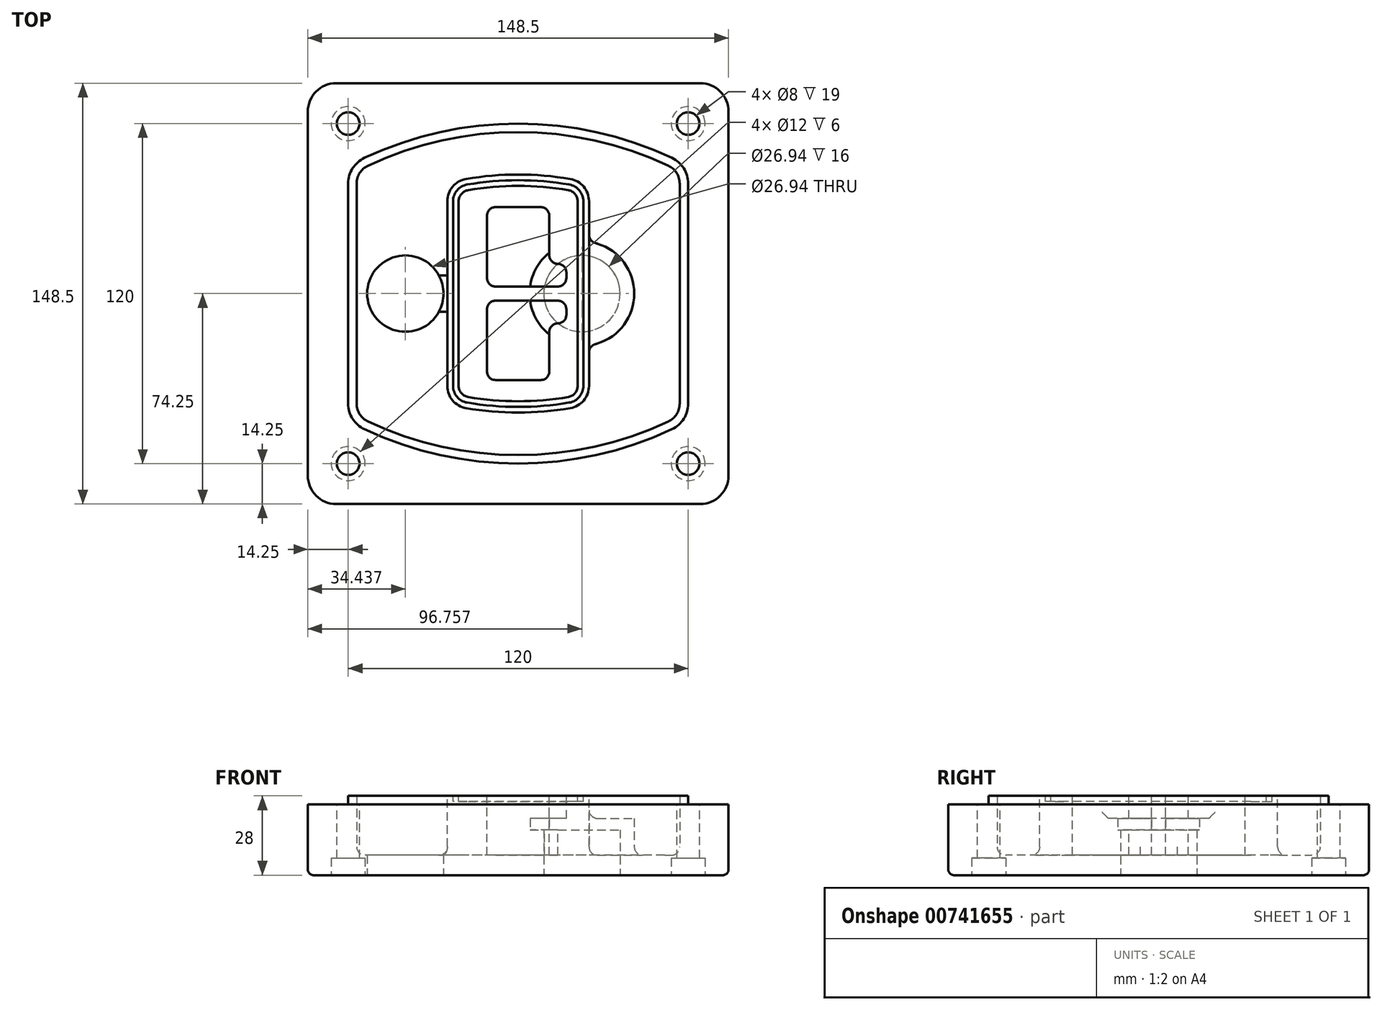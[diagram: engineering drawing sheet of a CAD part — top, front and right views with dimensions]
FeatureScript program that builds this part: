
annotation { "Feature Type Name" : "Feature", "Feature Type Description" : "" }
export const myFeature = defineFeature(function(context is Context, id is Id, definition is map)
    precondition{}
    {
        {
            var Q0;
            Q0=qCreatedBy(makeId("Top.planeOp"),FACE);
            var sketch = newSketch(context, id + "F0", { "sketchPlane" : qUnion([Q0])});
            skPoint(sketch, "E0.rect.middle", {"position": v(0, 0) * mm});
            skLineSegment(sketch, "E1.bottom", {"start": v(-64.25, -74.25) * mm, "end": v(64.25, -74.25) * mm});
            skLineSegment(sketch, "E1.top", {"start": v(-64.25, 74.25) * mm, "end": v(64.25, 74.25) * mm});
            skLineSegment(sketch, "E1.left", {"start": v(-74.25, -64.25) * mm, "end": v(-74.25, 64.25) * mm});
            skLineSegment(sketch, "E1.right", {"start": v(74.25, -64.25) * mm, "end": v(74.25, 64.25) * mm});
            skLineSegment(sketch, "E2", {"start": v(-74.25, 74.25) * mm, "end": v(74.25, -74.25) * mm, "construction": true});
            skLineSegment(sketch, "E3", {"start": v(74.25, 74.25) * mm, "end": v(-74.25, -74.25) * mm, "construction": true});
            skCircle(sketch, "E4", {"center": v(-60, 60) * mm, "radius": 4 * mm});
            skCircle(sketch, "E5", {"center": v(60, 60) * mm, "radius": 4 * mm});
            skCircle(sketch, "E6", {"center": v(60, -60) * mm, "radius": 4 * mm});
            skCircle(sketch, "E7", {"center": v(-60, -60) * mm, "radius": 4 * mm});
            skLineSegment(sketch, "E8", {"start": v(-60, 60) * mm, "end": v(60, 60) * mm, "construction": true});
            skLineSegment(sketch, "E9", {"start": v(60, 60) * mm, "end": v(60, -60) * mm, "construction": true});
            skLineSegment(sketch, "E10", {"start": v(60, -60) * mm, "end": v(-60, -60) * mm, "construction": true});
            skLineSegment(sketch, "E11", {"start": v(-60, -60) * mm, "end": v(-60, 60) * mm, "construction": true});
            skLineSegment(sketch, "E12", {"start": v(-60, 38.83) * mm, "end": v(-60, -38.83) * mm});
            skLineSegment(sketch, "E13", {"start": v(60, 38.83) * mm, "end": v(60, -38.83) * mm});
            skArc(sketch, "E14", {"start": v(54.26, 47.88) * mm, "mid": v(0, 60) * mm, "end": v(-54.26, 47.88) * mm});
            skArc(sketch, "E15", {"start": v(-54.26, -47.88) * mm, "mid": v(0, -60) * mm, "end": v(54.26, -47.88) * mm});
            skLineSegment(sketch, "E16", {"start": v(-60, 0) * mm, "end": v(60, 0) * mm, "construction": true});
            skPoint(sketch, "E17.visualSharp", {"position": v(-60, -45) * mm});
            skArc(sketch, "E17.filletArc", {"start": v(-60, -38.83) * mm, "mid": v(-58.44, -44.2) * mm, "end": v(-54.26, -47.88) * mm});
            skPoint(sketch, "E18.visualSharp", {"position": v(-60, 45) * mm});
            skArc(sketch, "E18.filletArc", {"start": v(-54.26, 47.88) * mm, "mid": v(-58.44, 44.2) * mm, "end": v(-60, 38.83) * mm});
            skPoint(sketch, "E19.visualSharp", {"position": v(60, 45) * mm});
            skArc(sketch, "E19.filletArc", {"start": v(60, 38.83) * mm, "mid": v(58.44, 44.2) * mm, "end": v(54.26, 47.88) * mm});
            skPoint(sketch, "E20.visualSharp", {"position": v(60, -45) * mm});
            skArc(sketch, "E20.filletArc", {"start": v(54.26, -47.88) * mm, "mid": v(58.44, -44.2) * mm, "end": v(60, -38.83) * mm});
            skPoint(sketch, "E21.visualSharp", {"position": v(-74.25, 74.25) * mm});
            skArc(sketch, "E21.filletArc", {"start": v(-64.25, 74.25) * mm, "mid": v(-71.32, 71.32) * mm, "end": v(-74.25, 64.25) * mm});
            skPoint(sketch, "E22.visualSharp", {"position": v(74.25, 74.25) * mm});
            skArc(sketch, "E22.filletArc", {"start": v(74.25, 64.25) * mm, "mid": v(71.32, 71.32) * mm, "end": v(64.25, 74.25) * mm});
            skPoint(sketch, "E23.visualSharp", {"position": v(74.25, -74.25) * mm});
            skArc(sketch, "E23.filletArc", {"start": v(64.25, -74.25) * mm, "mid": v(71.32, -71.32) * mm, "end": v(74.25, -64.25) * mm});
            skPoint(sketch, "E24.visualSharp", {"position": v(-74.25, -74.25) * mm});
            skArc(sketch, "E24.filletArc", {"start": v(-74.25, -64.25) * mm, "mid": v(-71.32, -71.32) * mm, "end": v(-64.25, -74.25) * mm});
            skArc(sketch, "E25.0", {"start": v(57, 38.83) * mm, "mid": v(55.9, 42.58) * mm, "end": v(52.98, 45.17) * mm});
            skLineSegment(sketch, "E25.1", {"start": v(57, 38.83) * mm, "end": v(57, -38.83) * mm});
            skArc(sketch, "E25.2", {"start": v(52.98, -45.17) * mm, "mid": v(55.9, -42.58) * mm, "end": v(57, -38.83) * mm});
            skArc(sketch, "E25.3", {"start": v(-52.98, -45.17) * mm, "mid": v(0, -57) * mm, "end": v(52.98, -45.17) * mm});
            skArc(sketch, "E25.4", {"start": v(-57, -38.83) * mm, "mid": v(-55.9, -42.58) * mm, "end": v(-52.98, -45.17) * mm});
            skArc(sketch, "E25.5", {"start": v(52.98, 45.17) * mm, "mid": v(0, 57) * mm, "end": v(-52.98, 45.17) * mm});
            skLineSegment(sketch, "E25.6", {"start": v(-57, 38.83) * mm, "end": v(-57, -38.83) * mm});
            skArc(sketch, "E25.7", {"start": v(-52.98, 45.17) * mm, "mid": v(-55.9, 42.58) * mm, "end": v(-57, 38.83) * mm});
            skArc(sketch, "E26.0", {"start": v(-55.96, 51.5) * mm, "mid": v(-61.82, 46.33) * mm, "end": v(-64, 38.83) * mm});
            skArc(sketch, "E26.1", {"start": v(55.96, 51.5) * mm, "mid": v(0, 64) * mm, "end": v(-55.96, 51.5) * mm});
            skArc(sketch, "E26.2", {"start": v(64, 38.83) * mm, "mid": v(61.82, 46.33) * mm, "end": v(55.96, 51.5) * mm});
            skLineSegment(sketch, "E26.3", {"start": v(64, 38.83) * mm, "end": v(64, -38.83) * mm});
            skArc(sketch, "E26.4", {"start": v(55.96, -51.5) * mm, "mid": v(61.82, -46.33) * mm, "end": v(64, -38.83) * mm});
            skLineSegment(sketch, "E26.5", {"start": v(-64, 38.83) * mm, "end": v(-64, -38.83) * mm});
            skArc(sketch, "E26.6", {"start": v(-55.96, -51.5) * mm, "mid": v(0, -64) * mm, "end": v(55.96, -51.5) * mm});
            skArc(sketch, "E26.7", {"start": v(-64, -38.83) * mm, "mid": v(-61.82, -46.33) * mm, "end": v(-55.96, -51.5) * mm});
            skSolve(sketch);
        }
        {
            var Q0;
            Q0=makeQuery(id+"F0.imprint","IMPRINT",FACE,{"disambiguationData":[TD([[makeQuery(id+"F0.imprint","IMPRINT",EDGE,{"derivedFrom":sQuery(id+"F0.wireOp",EDGE,"E1.bottom")}),1.0]])]});
            var Q1;
            Q1=makeQuery(id+"F0.imprint","IMPRINT",FACE,{"disambiguationData":[TD([[makeQuery(id+"F0.imprint","IMPRINT",EDGE,{"derivedFrom":sQuery(id+"F0.wireOp",EDGE,"E12")}),1.0]])]});
            var Q2;
            Q2=makeQuery(id+"F0.imprint","IMPRINT",FACE,{"disambiguationData":[TD([[makeQuery(id+"F0.imprint","IMPRINT",EDGE,{"derivedFrom":sQuery(id+"F0.wireOp",EDGE,"E25.0")}),1.0]])]});
            var Q3;
            Q3=makeQuery(id+"F0.imprint","IMPRINT",FACE,{"disambiguationData":[TD([[makeQuery(id+"F0.imprint","IMPRINT",EDGE,{"derivedFrom":sQuery(id+"F0.wireOp",EDGE,"E12")}),-1.0]])]});
            extrude(context, id + "F1", {"entities" : qUnion([Q0, Q1, Q2, Q3]), "oppositeDirection" : true, "depth" : 25 * mm, "offsetDistance" : 25 * mm});
        }
        {
            var Q0;
            Q0=makeQuery(id+"F0.imprint","IMPRINT",FACE,{"disambiguationData":[TD([[makeQuery(id+"F0.imprint","IMPRINT",EDGE,{"derivedFrom":sQuery(id+"F0.wireOp",EDGE,"E12")}),1.0]])]});
            extrude(context, id + "F2", {"entities" : qUnion([Q0]), "operationType" : NewBodyOperationType.ADD, "depth" : 3 * mm, "offsetDistance" : 25 * mm});
        }
        {
            var Q0;
            Q0=makeQuery(id+"F0.imprint","IMPRINT",FACE,{"disambiguationData":[TD([[makeQuery(id+"F0.imprint","IMPRINT",EDGE,{"derivedFrom":sQuery(id+"F0.wireOp",EDGE,"E25.0")}),1.0]])]});
            extrude(context, id + "F3", {"entities" : qUnion([Q0]), "operationType" : NewBodyOperationType.REMOVE, "oppositeDirection" : true, "depth" : 18 * mm, "offsetDistance" : 25 * mm});
        }
        {
            var Q0;
            Q0=makeQuery(id+"F2.opExtrude","CAP_FACE",FACE,{"disambiguationData":[OSD([sQuery(id+"F0.wireOp",EDGE,"E12"),sQuery(id+"F0.wireOp",EDGE,"E13"),sQuery(id+"F0.wireOp",EDGE,"E14"),sQuery(id+"F0.wireOp",EDGE,"E15"),sQuery(id+"F0.wireOp",EDGE,"E17.filletArc"),sQuery(id+"F0.wireOp",EDGE,"E18.filletArc"),sQuery(id+"F0.wireOp",EDGE,"E19.filletArc"),sQuery(id+"F0.wireOp",EDGE,"E20.filletArc"),sQuery(id+"F0.wireOp",EDGE,"E25.0"),sQuery(id+"F0.wireOp",EDGE,"E25.1"),sQuery(id+"F0.wireOp",EDGE,"E25.2"),sQuery(id+"F0.wireOp",EDGE,"E25.3"),sQuery(id+"F0.wireOp",EDGE,"E25.4"),sQuery(id+"F0.wireOp",EDGE,"E25.5"),sQuery(id+"F0.wireOp",EDGE,"E25.6"),sQuery(id+"F0.wireOp",EDGE,"E25.7")])],"isStart":false});
            var sketch = newSketch(context, id + "F4", { "sketchPlane" : qUnion([Q0])});
            skArc(sketch, "E27.0", {"start": v(-18.34, -40.45) * mm, "mid": v(0, -42) * mm, "end": v(18.34, -40.45) * mm});
            skArc(sketch, "E28.0", {"start": v(18.34, 40.45) * mm, "mid": v(0, 42) * mm, "end": v(-18.34, 40.45) * mm});
            skLineSegment(sketch, "E29", {"start": v(-25, 32.57) * mm, "end": v(-25, -32.57) * mm});
            skLineSegment(sketch, "E30", {"start": v(25, 32.57) * mm, "end": v(25, -32.57) * mm});
            skLineSegment(sketch, "E31", {"start": v(-25, 39.1) * mm, "end": v(25, 39.1) * mm, "construction": true});
            skLineSegment(sketch, "E32", {"start": v(-25, -39.1) * mm, "end": v(25, -39.1) * mm, "construction": true});
            skPoint(sketch, "E33.visualSharp", {"position": v(-25, 39.1) * mm});
            skArc(sketch, "E33.filletArc", {"start": v(-18.34, 40.45) * mm, "mid": v(-23.11, 37.73) * mm, "end": v(-25, 32.57) * mm});
            skPoint(sketch, "E34.visualSharp", {"position": v(25, 39.1) * mm});
            skArc(sketch, "E34.filletArc", {"start": v(25, 32.57) * mm, "mid": v(23.11, 37.73) * mm, "end": v(18.34, 40.45) * mm});
            skPoint(sketch, "E35.visualSharp", {"position": v(25, -39.1) * mm});
            skArc(sketch, "E35.filletArc", {"start": v(18.34, -40.45) * mm, "mid": v(23.11, -37.73) * mm, "end": v(25, -32.57) * mm});
            skPoint(sketch, "E36.visualSharp", {"position": v(-25, -39.1) * mm});
            skArc(sketch, "E36.filletArc", {"start": v(-25, -32.57) * mm, "mid": v(-23.11, -37.73) * mm, "end": v(-18.34, -40.45) * mm});
            skArc(sketch, "E37.0", {"start": v(52.98, 45.17) * mm, "mid": v(0, 57) * mm, "end": v(-52.98, 45.17) * mm});
            skArc(sketch, "E37.1", {"start": v(-52.98, 45.17) * mm, "mid": v(-55.9, 42.58) * mm, "end": v(-57, 38.83) * mm});
            skLineSegment(sketch, "E37.2", {"start": v(-57, 38.83) * mm, "end": v(-57, -38.83) * mm});
            skArc(sketch, "E37.3", {"start": v(-57, -38.83) * mm, "mid": v(-55.9, -42.58) * mm, "end": v(-52.98, -45.17) * mm});
            skArc(sketch, "E37.4", {"start": v(-52.98, -45.17) * mm, "mid": v(0, -57) * mm, "end": v(52.98, -45.17) * mm});
            skArc(sketch, "E37.5", {"start": v(52.98, -45.17) * mm, "mid": v(55.9, -42.58) * mm, "end": v(57, -38.83) * mm});
            skLineSegment(sketch, "E37.6", {"start": v(57, 38.83) * mm, "end": v(57, -38.83) * mm});
            skArc(sketch, "E37.7", {"start": v(57, 38.83) * mm, "mid": v(55.9, 42.58) * mm, "end": v(52.98, 45.17) * mm});
            skLineSegment(sketch, "E38.0", {"start": v(23, 32.57) * mm, "end": v(23, -32.57) * mm});
            skArc(sketch, "E38.1", {"start": v(18, -38.48) * mm, "mid": v(21.58, -36.44) * mm, "end": v(23, -32.57) * mm});
            skArc(sketch, "E38.2", {"start": v(-18, -38.48) * mm, "mid": v(0, -40) * mm, "end": v(18, -38.48) * mm});
            skArc(sketch, "E38.3", {"start": v(-23, -32.57) * mm, "mid": v(-21.58, -36.44) * mm, "end": v(-18, -38.48) * mm});
            skLineSegment(sketch, "E38.4", {"start": v(-23, 32.57) * mm, "end": v(-23, -32.57) * mm});
            skArc(sketch, "E38.5", {"start": v(23, 32.57) * mm, "mid": v(21.58, 36.44) * mm, "end": v(18, 38.48) * mm});
            skArc(sketch, "E38.6", {"start": v(-18, 38.48) * mm, "mid": v(-21.58, 36.44) * mm, "end": v(-23, 32.57) * mm});
            skArc(sketch, "E38.7", {"start": v(18, 38.48) * mm, "mid": v(0, 40) * mm, "end": v(-18, 38.48) * mm});
            skArc(sketch, "E39.0", {"start": v(21, 32.57) * mm, "mid": v(20.06, 35.15) * mm, "end": v(17.67, 36.5) * mm});
            skLineSegment(sketch, "E39.1", {"start": v(21, 32.57) * mm, "end": v(21, -32.57) * mm});
            skArc(sketch, "E39.2", {"start": v(17.67, -36.5) * mm, "mid": v(20.06, -35.15) * mm, "end": v(21, -32.57) * mm});
            skArc(sketch, "E39.3", {"start": v(-17.67, -36.5) * mm, "mid": v(0, -38) * mm, "end": v(17.67, -36.5) * mm});
            skArc(sketch, "E39.4", {"start": v(-21, -32.57) * mm, "mid": v(-20.06, -35.15) * mm, "end": v(-17.67, -36.5) * mm});
            skArc(sketch, "E39.5", {"start": v(17.67, 36.5) * mm, "mid": v(0, 38) * mm, "end": v(-17.67, 36.5) * mm});
            skLineSegment(sketch, "E39.6", {"start": v(-21, 32.57) * mm, "end": v(-21, -32.57) * mm});
            skArc(sketch, "E39.7", {"start": v(-17.67, 36.5) * mm, "mid": v(-20.06, 35.15) * mm, "end": v(-21, 32.57) * mm});
            skLineSegment(sketch, "E40", {"start": v(-25, 0) * mm, "end": v(25, 0) * mm, "construction": true});
            skLineSegment(sketch, "E41", {"start": v(-11, 5.5) * mm, "end": v(-11, 27.5) * mm});
            skLineSegment(sketch, "E42", {"start": v(-8, 30.5) * mm, "end": v(8, 30.5) * mm});
            skLineSegment(sketch, "E43", {"start": v(11, 27.5) * mm, "end": v(11, 13.5) * mm});
            skLineSegment(sketch, "E44", {"start": v(14, 10.5) * mm, "end": v(14, 10.5) * mm});
            skLineSegment(sketch, "E45", {"start": v(17, 7.5) * mm, "end": v(17, 5.5) * mm});
            skLineSegment(sketch, "E46", {"start": v(14, 2.5) * mm, "end": v(-8, 2.5) * mm});
            skPoint(sketch, "E47.visualSharp", {"position": v(-11, 30.5) * mm});
            skArc(sketch, "E47.filletArc", {"start": v(-8, 30.5) * mm, "mid": v(-10.12, 29.62) * mm, "end": v(-11, 27.5) * mm});
            skPoint(sketch, "E48.visualSharp", {"position": v(11, 30.5) * mm});
            skArc(sketch, "E48.filletArc", {"start": v(11, 27.5) * mm, "mid": v(10.12, 29.62) * mm, "end": v(8, 30.5) * mm});
            skPoint(sketch, "E49.visualSharp", {"position": v(11, 10.5) * mm});
            skArc(sketch, "E49.filletArc", {"start": v(11, 13.5) * mm, "mid": v(11.88, 11.38) * mm, "end": v(14, 10.5) * mm});
            skPoint(sketch, "E50.visualSharp", {"position": v(17, 10.5) * mm});
            skArc(sketch, "E50.filletArc", {"start": v(17, 7.5) * mm, "mid": v(16.12, 9.62) * mm, "end": v(14, 10.5) * mm});
            skPoint(sketch, "E51.visualSharp", {"position": v(17, 2.5) * mm});
            skArc(sketch, "E51.filletArc", {"start": v(14, 2.5) * mm, "mid": v(16.12, 3.38) * mm, "end": v(17, 5.5) * mm});
            skPoint(sketch, "E52.visualSharp", {"position": v(-11, 2.5) * mm});
            skArc(sketch, "E52.filletArc", {"start": v(-11, 5.5) * mm, "mid": v(-10.12, 3.38) * mm, "end": v(-8, 2.5) * mm});
            skLineSegment(sketch, "E53.0.MirrorCS", {"start": v(14, -2.5) * mm, "end": v(-8, -2.5) * mm});
            skArc(sketch, "E54.0.MirrorCS", {"start": v(-11, -5.5) * mm, "mid": v(-10.12, -3.38) * mm, "end": v(-8, -2.5) * mm});
            skLineSegment(sketch, "E55.0.MirrorCS", {"start": v(-11, -5.5) * mm, "end": v(-11, -27.5) * mm});
            skArc(sketch, "E56.0.MirrorCS", {"start": v(-8, -30.5) * mm, "mid": v(-10.12, -29.62) * mm, "end": v(-11, -27.5) * mm});
            skLineSegment(sketch, "E57.0.MirrorCS", {"start": v(-8, -30.5) * mm, "end": v(8, -30.5) * mm});
            skArc(sketch, "E58.0.MirrorCS", {"start": v(11, -27.5) * mm, "mid": v(10.12, -29.62) * mm, "end": v(8, -30.5) * mm});
            skLineSegment(sketch, "E59.0.MirrorCS", {"start": v(11, -27.5) * mm, "end": v(11, -13.5) * mm});
            skArc(sketch, "E60.0.MirrorCS", {"start": v(11, -13.5) * mm, "mid": v(11.88, -11.38) * mm, "end": v(14, -10.5) * mm});
            skArc(sketch, "E61.0.MirrorCS", {"start": v(17, -7.5) * mm, "mid": v(16.12, -9.62) * mm, "end": v(14, -10.5) * mm});
            skLineSegment(sketch, "E62.0.MirrorCS", {"start": v(17, -7.5) * mm, "end": v(17, -5.5) * mm});
            skArc(sketch, "E63.0.MirrorCS", {"start": v(14, -2.5) * mm, "mid": v(16.12, -3.38) * mm, "end": v(17, -5.5) * mm});
            skSolve(sketch);
        }
        {
            var Q0;
            Q0=makeQuery(id+"F4.imprint","IMPRINT",FACE,{"disambiguationData":[TD([[makeQuery(id+"F4.imprint","IMPRINT",EDGE,{"derivedFrom":sQuery(id+"F4.wireOp",EDGE,"E27.0")}),1.0]])]});
            var Q1;
            Q1=makeQuery(id+"F4.imprint","IMPRINT",FACE,{"disambiguationData":[TD([[makeQuery(id+"F4.imprint","IMPRINT",EDGE,{"derivedFrom":sQuery(id+"F4.wireOp",EDGE,"E38.0")}),-1.0]])]});
            var Q2;
            Q2=makeQuery(id+"F4.imprint","IMPRINT",FACE,{"disambiguationData":[TD([[makeQuery(id+"F4.imprint","IMPRINT",EDGE,{"derivedFrom":sQuery(id+"F4.wireOp",EDGE,"E39.0")}),1.0]])]});
            extrude(context, id + "F5", {"entities" : qUnion([Q0, Q1, Q2]), "operationType" : NewBodyOperationType.ADD, "endBound" : BoundingType.UP_TO_NEXT, "oppositeDirection" : true, "depth" : 25 * mm});
        }
        {
            var Q0;
            Q0=makeQuery(id+"F4.imprint","IMPRINT",FACE,{"disambiguationData":[TD([[makeQuery(id+"F4.imprint","IMPRINT",EDGE,{"derivedFrom":sQuery(id+"F4.wireOp",EDGE,"E38.0")}),-1.0]])]});
            extrude(context, id + "F6", {"entities" : qUnion([Q0]), "operationType" : NewBodyOperationType.REMOVE, "oppositeDirection" : true, "depth" : 2 * mm});
        }
        {
            var Q0;
            Q0=makeQuery(id+"F1.opExtrude","CAP_FACE",FACE,{"disambiguationData":[OSD([sQuery(id+"F0.wireOp",EDGE,"E1.bottom"),sQuery(id+"F0.wireOp",EDGE,"E1.top"),sQuery(id+"F0.wireOp",EDGE,"E1.left"),sQuery(id+"F0.wireOp",EDGE,"E1.right"),sQuery(id+"F0.wireOp",EDGE,"E4"),sQuery(id+"F0.wireOp",EDGE,"E5"),sQuery(id+"F0.wireOp",EDGE,"E6"),sQuery(id+"F0.wireOp",EDGE,"E7"),sQuery(id+"F0.wireOp",EDGE,"E21.filletArc"),sQuery(id+"F0.wireOp",EDGE,"E22.filletArc"),sQuery(id+"F0.wireOp",EDGE,"E23.filletArc"),sQuery(id+"F0.wireOp",EDGE,"E24.filletArc")])],"isStart":false});
            var sketch = newSketch(context, id + "F7", { "sketchPlane" : qUnion([Q0])});
            skCircle(sketch, "E64", {"center": v(22.5, 0) * mm, "radius": 13.47 * mm});
            skCircle(sketch, "E65", {"center": v(-39.81, 0) * mm, "radius": 13.47 * mm});
            skLineSegment(sketch, "E66", {"start": v(74.25, 0) * mm, "end": v(-74.25, 0) * mm, "construction": true});
            skCircle(sketch, "E67", {"center": v(22.5, 0) * mm, "radius": 18.47 * mm});
            skCircle(sketch, "E68", {"center": v(60, -60) * mm, "radius": 6 * mm});
            skCircle(sketch, "E69", {"center": v(-60, -60) * mm, "radius": 6 * mm});
            skCircle(sketch, "E70", {"center": v(-60, 60) * mm, "radius": 6 * mm});
            skCircle(sketch, "E71", {"center": v(60, 60) * mm, "radius": 6 * mm});
            skLineSegment(sketch, "E72", {"start": v(-33.38, -74.25) * mm, "end": v(-21.63, -92.25) * mm});
            skLineSegment(sketch, "E73", {"start": v(-21.63, -92.25) * mm, "end": v(-21.63, -104.25) * mm});
            skLineSegment(sketch, "E74", {"start": v(20.12, -74.25) * mm, "end": v(8.37, -92.25) * mm});
            skLineSegment(sketch, "E75", {"start": v(8.37, -92.25) * mm, "end": v(8.37, -104.25) * mm});
            skArc(sketch, "E76", {"start": v(-21.63, -104.25) * mm, "mid": v(-6.63, -119.25) * mm, "end": v(8.37, -104.25) * mm});
            skLineSegment(sketch, "E77", {"start": v(-74.25, 0) * mm, "end": v(74.25, 0) * mm});
            skCircle(sketch, "E78", {"center": v(-6.63, -104.25) * mm, "radius": 6 * mm});
            skSolve(sketch);
        }
        {
            var Q0;
            {var subQ1=sQuery(id+"F7.wireOp",EDGE,"E66");var subQ4=sQuery(id+"F7.wireOp",EDGE,"E64");var subQ6=makeQuery(id+"F7.imprint","INTERSECT",VERTEX,{"disambiguationData":[OD(0.0)],"derivedFrom":[subQ4,subQ1]});Q0=makeQuery(id+"F7.imprint","IMPRINT",FACE,{"disambiguationData":[TD([[makeQuery(id+"F7.imprint","IMPRINT",EDGE,{"disambiguationData":[TD([[subQ6,-1.0]])],"derivedFrom":subQ4}),-1.0]])]});}
            var Q1;
            {var subQ0=sQuery(id+"F7.wireOp",EDGE,"E66");var subQ1=sQuery(id+"F7.wireOp",EDGE,"E64");var subQ3=makeQuery(id+"F7.imprint","INTERSECT",VERTEX,{"disambiguationData":[OD(0.0)],"derivedFrom":[subQ1,subQ0]});Q1=makeQuery(id+"F7.imprint","IMPRINT",FACE,{"disambiguationData":[TD([[makeQuery(id+"F7.imprint","IMPRINT",EDGE,{"disambiguationData":[TD([[subQ3,-1.0]])],"derivedFrom":subQ1}),1.0]])]});}
            var Q2;
            {var subQ0=sQuery(id+"F7.wireOp",EDGE,"E66");var subQ1=sQuery(id+"F7.wireOp",EDGE,"E64");var subQ3=makeQuery(id+"F7.imprint","INTERSECT",VERTEX,{"disambiguationData":[OD(0.0)],"derivedFrom":[subQ1,subQ0]});Q2=makeQuery(id+"F7.imprint","IMPRINT",FACE,{"disambiguationData":[TD([[makeQuery(id+"F7.imprint","IMPRINT",EDGE,{"disambiguationData":[TD([[subQ3,1.0]])],"derivedFrom":subQ1}),1.0]])]});}
            var Q3;
            {var subQ1=sQuery(id+"F7.wireOp",EDGE,"E66");var subQ4=sQuery(id+"F7.wireOp",EDGE,"E64");var subQ6=makeQuery(id+"F7.imprint","INTERSECT",VERTEX,{"disambiguationData":[OD(0.0)],"derivedFrom":[subQ4,subQ1]});Q3=makeQuery(id+"F7.imprint","IMPRINT",FACE,{"disambiguationData":[TD([[makeQuery(id+"F7.imprint","IMPRINT",EDGE,{"disambiguationData":[TD([[subQ6,1.0]])],"derivedFrom":subQ4}),-1.0]])]});}
            extrude(context, id + "F8", {"entities" : qUnion([Q0, Q1, Q2, Q3]), "operationType" : NewBodyOperationType.ADD, "oppositeDirection" : true, "depth" : 20 * mm});
        }
        {
            var Q0;
            {var subQ0=sQuery(id+"F7.wireOp",EDGE,"E66");var subQ1=sQuery(id+"F7.wireOp",EDGE,"E64");var subQ3=makeQuery(id+"F7.imprint","INTERSECT",VERTEX,{"disambiguationData":[OD(0.0)],"derivedFrom":[subQ1,subQ0]});Q0=makeQuery(id+"F7.imprint","IMPRINT",FACE,{"disambiguationData":[TD([[makeQuery(id+"F7.imprint","IMPRINT",EDGE,{"disambiguationData":[TD([[subQ3,-1.0]])],"derivedFrom":subQ1}),1.0]])]});}
            var Q1;
            {var subQ0=sQuery(id+"F7.wireOp",EDGE,"E66");var subQ1=sQuery(id+"F7.wireOp",EDGE,"E64");var subQ3=makeQuery(id+"F7.imprint","INTERSECT",VERTEX,{"disambiguationData":[OD(0.0)],"derivedFrom":[subQ1,subQ0]});Q1=makeQuery(id+"F7.imprint","IMPRINT",FACE,{"disambiguationData":[TD([[makeQuery(id+"F7.imprint","IMPRINT",EDGE,{"disambiguationData":[TD([[subQ3,1.0]])],"derivedFrom":subQ1}),1.0]])]});}
            extrude(context, id + "F9", {"entities" : qUnion([Q0, Q1]), "operationType" : NewBodyOperationType.REMOVE, "oppositeDirection" : true, "depth" : 16 * mm});
        }
        {
            var Q0;
            {var subQ0=sQuery(id+"F7.wireOp",EDGE,"E66");var subQ1=sQuery(id+"F7.wireOp",EDGE,"E65");var subQ3=makeQuery(id+"F7.imprint","INTERSECT",VERTEX,{"disambiguationData":[OD(0.0)],"derivedFrom":[subQ1,subQ0]});Q0=makeQuery(id+"F7.imprint","IMPRINT",FACE,{"disambiguationData":[TD([[makeQuery(id+"F7.imprint","IMPRINT",EDGE,{"disambiguationData":[TD([[subQ3,-1.0]])],"derivedFrom":subQ1}),1.0]])]});}
            var Q1;
            {var subQ0=sQuery(id+"F7.wireOp",EDGE,"E66");var subQ1=sQuery(id+"F7.wireOp",EDGE,"E65");var subQ3=makeQuery(id+"F7.imprint","INTERSECT",VERTEX,{"disambiguationData":[OD(0.0)],"derivedFrom":[subQ1,subQ0]});Q1=makeQuery(id+"F7.imprint","IMPRINT",FACE,{"disambiguationData":[TD([[makeQuery(id+"F7.imprint","IMPRINT",EDGE,{"disambiguationData":[TD([[subQ3,1.0]])],"derivedFrom":subQ1}),1.0]])]});}
            extrude(context, id + "F10", {"entities" : qUnion([Q0, Q1]), "operationType" : NewBodyOperationType.REMOVE, "oppositeDirection" : true, "depth" : 25 * mm});
        }
        {
            var Q0;
            Q0=makeQuery(id+"F7.imprint","IMPRINT",FACE,{"disambiguationData":[TD([[makeQuery(id+"F7.imprint","IMPRINT",EDGE,{"derivedFrom":sQuery(id+"F7.wireOp",EDGE,"E68")}),1.0]])]});
            var Q1;
            Q1=makeQuery(id+"F7.imprint","IMPRINT",FACE,{"disambiguationData":[TD([[makeQuery(id+"F7.imprint","IMPRINT",EDGE,{"derivedFrom":makeQuery(id+"F1.opExtrude","CAP_EDGE",EDGE,{"disambiguationData":[OSD([sQuery(id+"F0.wireOp",EDGE,"E5")])],"isStart":false})}),-1.0]])]});
            var Q2;
            Q2=makeQuery(id+"F7.imprint","IMPRINT",FACE,{"disambiguationData":[TD([[makeQuery(id+"F7.imprint","IMPRINT",EDGE,{"derivedFrom":sQuery(id+"F7.wireOp",EDGE,"E69")}),1.0]])]});
            var Q3;
            Q3=makeQuery(id+"F7.imprint","IMPRINT",FACE,{"disambiguationData":[TD([[makeQuery(id+"F7.imprint","IMPRINT",EDGE,{"derivedFrom":makeQuery(id+"F1.opExtrude","CAP_EDGE",EDGE,{"disambiguationData":[OSD([sQuery(id+"F0.wireOp",EDGE,"E4")])],"isStart":false})}),-1.0]])]});
            var Q4;
            Q4=makeQuery(id+"F7.imprint","IMPRINT",FACE,{"disambiguationData":[TD([[makeQuery(id+"F7.imprint","IMPRINT",EDGE,{"derivedFrom":sQuery(id+"F7.wireOp",EDGE,"E70")}),1.0]])]});
            var Q5;
            Q5=makeQuery(id+"F7.imprint","IMPRINT",FACE,{"disambiguationData":[TD([[makeQuery(id+"F7.imprint","IMPRINT",EDGE,{"derivedFrom":makeQuery(id+"F1.opExtrude","CAP_EDGE",EDGE,{"disambiguationData":[OSD([sQuery(id+"F0.wireOp",EDGE,"E7")])],"isStart":false})}),-1.0]])]});
            var Q6;
            Q6=makeQuery(id+"F7.imprint","IMPRINT",FACE,{"disambiguationData":[TD([[makeQuery(id+"F7.imprint","IMPRINT",EDGE,{"derivedFrom":sQuery(id+"F7.wireOp",EDGE,"E71")}),1.0]])]});
            var Q7;
            Q7=makeQuery(id+"F7.imprint","IMPRINT",FACE,{"disambiguationData":[TD([[makeQuery(id+"F7.imprint","IMPRINT",EDGE,{"derivedFrom":makeQuery(id+"F1.opExtrude","CAP_EDGE",EDGE,{"disambiguationData":[OSD([sQuery(id+"F0.wireOp",EDGE,"E6")])],"isStart":false})}),-1.0]])]});
            extrude(context, id + "F11", {"entities" : qUnion([Q0, Q1, Q2, Q3, Q4, Q5, Q6, Q7]), "operationType" : NewBodyOperationType.REMOVE, "oppositeDirection" : true, "depth" : 6 * mm});
        }
        {
            var Q0;
            Q0=makeQuery(id+"F9.boolean.opBoolean","COPY",FACE,{"derivedFrom":makeQuery(id+"F9.opExtrude","CAP_FACE",FACE,{"disambiguationData":[OSD([sQuery(id+"F7.wireOp",EDGE,"E64")])],"isStart":false})});
            var sketch = newSketch(context, id + "F12", { "sketchPlane" : qUnion([Q0])});
            skArc(sketch, "E79.0", {"start": v(11, 14.45) * mm, "mid": v(6.45, 9.13) * mm, "end": v(4.2, 2.5) * mm});
            skArc(sketch, "E79.1", {"start": v(4.2, -2.5) * mm, "mid": v(6.45, -9.13) * mm, "end": v(11, -14.45) * mm});
            skLineSegment(sketch, "E80", {"start": v(4.2, -2.5) * mm, "end": v(14, -2.5) * mm});
            skLineSegment(sketch, "E81.0", {"start": v(14, 2.5) * mm, "end": v(4.2, 2.5) * mm});
            skArc(sketch, "E81.1", {"start": v(14, 2.5) * mm, "mid": v(16.12, 3.38) * mm, "end": v(17, 5.5) * mm});
            skLineSegment(sketch, "E81.2", {"start": v(17, 7.5) * mm, "end": v(17, 5.5) * mm});
            skArc(sketch, "E81.3", {"start": v(17, 7.5) * mm, "mid": v(16.12, 9.62) * mm, "end": v(14, 10.5) * mm});
            skArc(sketch, "E81.4", {"start": v(11, 13.5) * mm, "mid": v(11.88, 11.38) * mm, "end": v(14, 10.5) * mm});
            skLineSegment(sketch, "E81.5", {"start": v(11, 14.45) * mm, "end": v(11, 13.5) * mm});
            skLineSegment(sketch, "E81.7", {"start": v(14, -2.5) * mm, "end": v(4.2, -2.5) * mm});
            skArc(sketch, "E81.8", {"start": v(14, -2.5) * mm, "mid": v(16.12, -3.38) * mm, "end": v(17, -5.5) * mm});
            skLineSegment(sketch, "E81.9", {"start": v(17, -7.5) * mm, "end": v(17, -5.5) * mm});
            skArc(sketch, "E81.10", {"start": v(17, -7.5) * mm, "mid": v(16.12, -9.62) * mm, "end": v(14, -10.5) * mm});
            skArc(sketch, "E81.11", {"start": v(11, -13.5) * mm, "mid": v(11.88, -11.38) * mm, "end": v(14, -10.5) * mm});
            skLineSegment(sketch, "E81.12", {"start": v(11, -14.45) * mm, "end": v(11, -13.5) * mm});
            skPoint(sketch, "E82.orphan", {"position": v(11, -27.5) * mm});
            skPoint(sketch, "E83.orphan", {"position": v(-8, -2.5) * mm});
            skPoint(sketch, "E84.orphan", {"position": v(-8, 2.5) * mm});
            skPoint(sketch, "E85.orphan", {"position": v(11, 27.5) * mm});
            skSolve(sketch);
        }
        {
            var Q0;
            {var subQ7=sQuery(id+"F12.wireOp",EDGE,"E79.0");var subQ14=sQuery(id+"F12.wireOp",EDGE,"E79.1");var subQ16=sQuery(id+"F12.wireOp",EDGE,"E81.1");var subQ18=sQuery(id+"F12.wireOp",EDGE,"E81.8");Q0=qUnion([makeQuery(id+"F12.imprint","IMPRINT",FACE,{"disambiguationData":[TD([[makeQuery(id+"F12.imprint","IMPRINT",EDGE,{"derivedFrom":subQ7}),1.0]])]}),makeQuery(id+"F12.imprint","IMPRINT",FACE,{"disambiguationData":[TD([[makeQuery(id+"F12.imprint","IMPRINT",EDGE,{"derivedFrom":subQ14}),1.0]])]}),makeQuery(id+"F12.imprint","IMPRINT",FACE,{"disambiguationData":[TD([[makeQuery(id+"F12.imprint","IMPRINT",EDGE,{"derivedFrom":subQ16}),1.0]])]}),makeQuery(id+"F12.imprint","IMPRINT",FACE,{"disambiguationData":[TD([[makeQuery(id+"F12.imprint","IMPRINT",EDGE,{"derivedFrom":subQ18}),-1.0]])]})]);}
            var Q1;
            Q1=makeQuery(id+"F5.boolean.opBoolean","SPLIT",FACE,{"disambiguationData":[TD([makeQuery(id+"F5.opExtrude","SWEPT_FACE",FACE,{"disambiguationData":[OSD([sQuery(id+"F4.wireOp",EDGE,"E41")])]})])],"derivedFrom":makeQuery(id+"F3.boolean.opBoolean","COPY",FACE,{"derivedFrom":makeQuery(id+"F3.opExtrude","CAP_FACE",FACE,{"disambiguationData":[OSD([sQuery(id+"F0.wireOp",EDGE,"E25.0"),sQuery(id+"F0.wireOp",EDGE,"E25.1"),sQuery(id+"F0.wireOp",EDGE,"E25.2"),sQuery(id+"F0.wireOp",EDGE,"E25.3"),sQuery(id+"F0.wireOp",EDGE,"E25.4"),sQuery(id+"F0.wireOp",EDGE,"E25.5"),sQuery(id+"F0.wireOp",EDGE,"E25.6"),sQuery(id+"F0.wireOp",EDGE,"E25.7")])],"isStart":false})})});
            extrude(context, id + "F13", {"entities" : qUnion([Q0]), "operationType" : NewBodyOperationType.REMOVE, "endBound" : BoundingType.UP_TO_SURFACE, "endBoundEntityFace" : qUnion([Q1]), "depth" : 25 * mm});
        }
        {
            var Q0;
            Q0=makeQuery(id+"F3.boolean.opBoolean","COPY",EDGE,{"derivedFrom":makeQuery(id+"F3.opExtrude","CAP_EDGE",EDGE,{"disambiguationData":[OSD([sQuery(id+"F0.wireOp",EDGE,"E25.6")])],"isStart":false})});
            var Q1;
            Q1=makeQuery(id+"F8.boolean.opBoolean","INTERSECT",EDGE,{"derivedFrom":[makeQuery(id+"F5.opExtrude","SWEPT_FACE",FACE,{"disambiguationData":[OSD([sQuery(id+"F4.wireOp",EDGE,"E30")])]}),makeQuery(id+"F8.opExtrude","CAP_FACE",FACE,{"disambiguationData":[OSD([sQuery(id+"F7.wireOp",EDGE,"E67")])],"isStart":false})]});
            var Q2;
            Q2=makeQuery(id+"F8.boolean.opBoolean","INTERSECT",EDGE,{"disambiguationData":[OD(1.0)],"derivedFrom":[makeQuery(id+"F5.opExtrude","SWEPT_FACE",FACE,{"disambiguationData":[OSD([sQuery(id+"F4.wireOp",EDGE,"E30")])]}),makeQuery(id+"F8.opExtrude","SWEPT_FACE",FACE,{"disambiguationData":[OSD([sQuery(id+"F7.wireOp",EDGE,"E67")])]})]});
            var Q3;
            {var subQ0=sQuery(id+"F4.wireOp",EDGE,"E30");Q3=makeQuery(id+"F8.boolean.opBoolean","SPLIT",EDGE,{"disambiguationData":[TD([makeQuery(id+"F5.opExtrude","SWEPT_FACE",FACE,{"disambiguationData":[OSD([sQuery(id+"F4.wireOp",EDGE,"E35.filletArc")])]})])],"derivedFrom":makeQuery(id+"F5.opExtrude","CAP_EDGE",EDGE,{"disambiguationData":[OSD([subQ0])],"isStart":false})});}
            var Q4;
            {var subQ0=sQuery(id+"F0.wireOp",EDGE,"E25.7");var subQ1=sQuery(id+"F0.wireOp",EDGE,"E25.1");var subQ2=sQuery(id+"F0.wireOp",EDGE,"E25.6");var subQ3=sQuery(id+"F0.wireOp",EDGE,"E25.5");var subQ4=sQuery(id+"F0.wireOp",EDGE,"E25.4");var subQ5=sQuery(id+"F0.wireOp",EDGE,"E25.0");var subQ6=sQuery(id+"F0.wireOp",EDGE,"E25.2");var subQ7=sQuery(id+"F0.wireOp",EDGE,"E25.3");Q4=makeQuery(id+"F8.boolean.opBoolean","INTERSECT",EDGE,{"derivedFrom":[makeQuery(id+"F5.boolean.opBoolean","SPLIT",FACE,{"disambiguationData":[TD([makeQuery(id+"F2.opExtrude","SWEPT_FACE",FACE,{"disambiguationData":[OSD([subQ5])]})])],"derivedFrom":makeQuery(id+"F3.boolean.opBoolean","COPY",FACE,{"derivedFrom":makeQuery(id+"F3.opExtrude","CAP_FACE",FACE,{"disambiguationData":[OSD([subQ5,subQ1,subQ6,subQ7,subQ4,subQ3,subQ2,subQ0])],"isStart":false})})}),makeQuery(id+"F8.opExtrude","SWEPT_FACE",FACE,{"disambiguationData":[OSD([sQuery(id+"F7.wireOp",EDGE,"E67")])]})]});}
            var Q5;
            Q5=makeQuery(id+"F8.boolean.opBoolean","INTERSECT",EDGE,{"disambiguationData":[OD(0.0)],"derivedFrom":[makeQuery(id+"F5.opExtrude","SWEPT_FACE",FACE,{"disambiguationData":[OSD([sQuery(id+"F4.wireOp",EDGE,"E30")])]}),makeQuery(id+"F8.opExtrude","SWEPT_FACE",FACE,{"disambiguationData":[OSD([sQuery(id+"F7.wireOp",EDGE,"E67")])]})]});
            fillet(context, id + "F14", {"entities" : qUnion([Q0, Q1, Q2, Q3, Q4, Q5]), "radius" : 3 * mm, "tangentPropagation" : true, "allowEdgeOverflow" : false});
        }
        {
            var Q0;
            Q0=makeQuery(id+"F1.opExtrude","CAP_EDGE",EDGE,{"disambiguationData":[OSD([sQuery(id+"F0.wireOp",EDGE,"E1.bottom")])],"isStart":false});
            fillet(context, id + "F15", {"entities" : qUnion([Q0]), "radius" : 2 * mm, "tangentPropagation" : true, "allowEdgeOverflow" : false});
        }
    });
